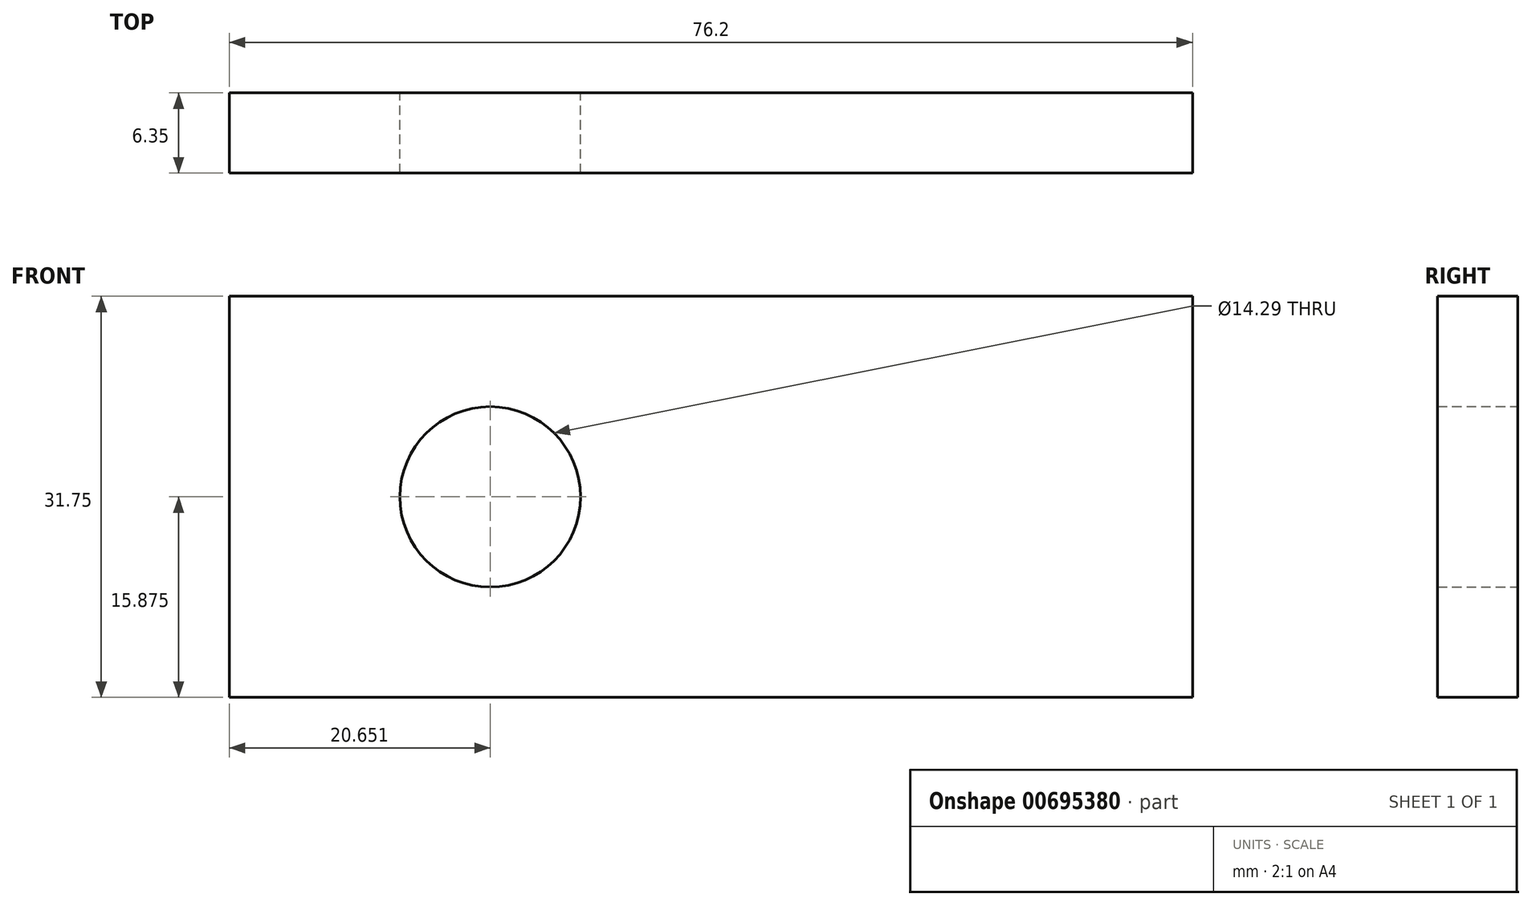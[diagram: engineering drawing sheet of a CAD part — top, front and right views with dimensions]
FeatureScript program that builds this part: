
annotation { "Feature Type Name" : "Feature", "Feature Type Description" : "" }
export const myFeature = defineFeature(function(context is Context, id is Id, definition is map)
    precondition{}
    {
        {
            var Q0;
            Q0=qCreatedBy(makeId("Front.planeOp"),FACE);
            var sketch = newSketch(context, id + "F0", { "sketchPlane" : qUnion([Q0])});
            skLineSegment(sketch, "E0.bottom", {"start": v(0, 0) * mm, "end": v(76.2, 0) * mm});
            skLineSegment(sketch, "E0.top", {"start": v(0, 31.75) * mm, "end": v(76.2, 31.75) * mm});
            skLineSegment(sketch, "E0.left", {"start": v(0, 0) * mm, "end": v(0, 31.75) * mm});
            skLineSegment(sketch, "E0.right", {"start": v(76.2, 0) * mm, "end": v(76.2, 31.75) * mm});
            skCircle(sketch, "E1", {"center": v(20.65, 15.88) * mm, "radius": 7.14 * mm});
            skPoint(sketch, "E1.centerSnap0", {"position": v(0, 15.88) * mm});
            skSolve(sketch);
        }
        {
            var Q0;
            Q0 = qSketchRegion(id + "F0", true);
            extrude(context, id + "F1", {"entities" : qUnion([Q0]), "depth" : 6.35 * mm, "offsetDistance" : 25.4 * mm});
        }
    });
